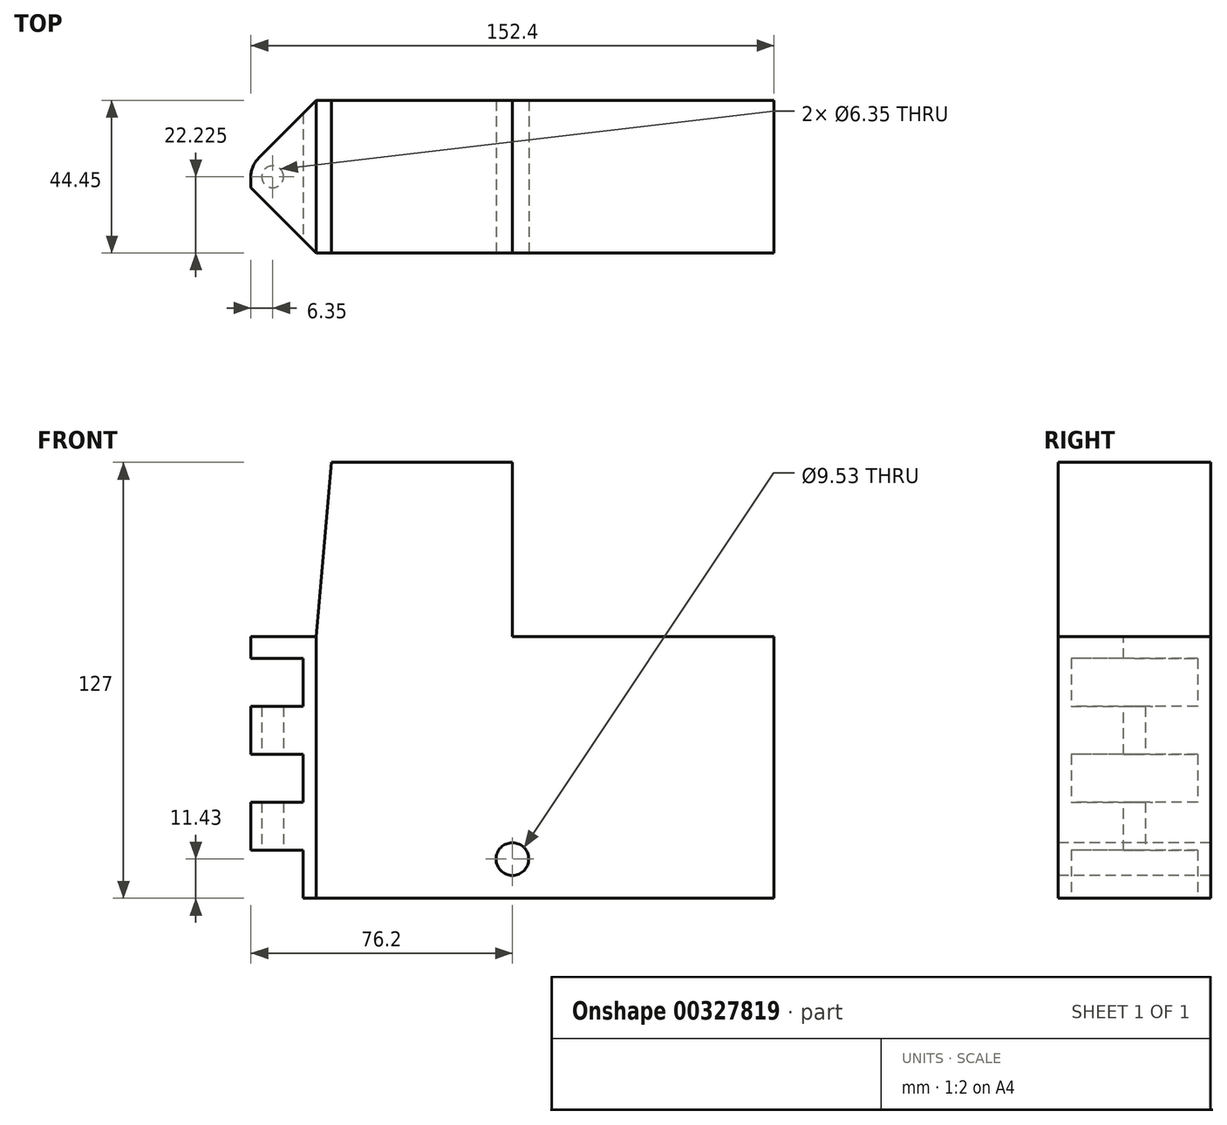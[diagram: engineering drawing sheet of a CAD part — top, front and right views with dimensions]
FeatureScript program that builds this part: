
annotation { "Feature Type Name" : "Feature", "Feature Type Description" : "" }
export const myFeature = defineFeature(function(context is Context, id is Id, definition is map)
    precondition{}
    {
        {
            var Q0;
            Q0=qCreatedBy(makeId("Front.planeOp"),FACE);
            var sketch = newSketch(context, id + "F0", { "sketchPlane" : qUnion([Q0])});
            skLineSegment(sketch, "E0.bottom", {"start": v(0, 0) * mm, "end": v(152.4, 0) * mm});
            skLineSegment(sketch, "E0.top", {"start": v(0, 76.2) * mm, "end": v(152.4, 76.2) * mm});
            skLineSegment(sketch, "E0.left", {"start": v(0, 0) * mm, "end": v(0, 76.2) * mm});
            skLineSegment(sketch, "E0.right", {"start": v(152.4, 0) * mm, "end": v(152.4, 76.2) * mm});
            skSolve(sketch);
        }
        {
            var Q0;
            Q0 = qSketchRegion(id + "F0", true);
            extrude(context, id + "F1", {"entities" : qUnion([Q0]), "depth" : 44.45 * mm});
        }
        {
            var Q0;
            Q0=makeQuery(id+"F1.opExtrude","CAP_FACE",FACE,{"disambiguationData":[OSD([sQuery(id+"F0.wireOp",EDGE,"E0.bottom"),sQuery(id+"F0.wireOp",EDGE,"E0.top"),sQuery(id+"F0.wireOp",EDGE,"E0.left"),sQuery(id+"F0.wireOp",EDGE,"E0.right")])],"isStart":false});
            var sketch = newSketch(context, id + "F2", { "sketchPlane" : qUnion([Q0])});
            skLineSegment(sketch, "E1.0", {"start": v(0, 0) * mm, "end": v(0, 76.2) * mm, "construction": true});
            skLineSegment(sketch, "E2.bottom", {"start": v(0, 0) * mm, "end": v(15.24, 0) * mm});
            skLineSegment(sketch, "E2.top", {"start": v(0, 13.97) * mm, "end": v(15.24, 13.97) * mm});
            skLineSegment(sketch, "E2.left", {"start": v(0, 0) * mm, "end": v(0, 13.97) * mm});
            skLineSegment(sketch, "E2.right", {"start": v(15.24, 0) * mm, "end": v(15.24, 13.97) * mm});
            skLineSegment(sketch, "E3.bottom", {"start": v(0, 27.94) * mm, "end": v(15.24, 27.94) * mm});
            skLineSegment(sketch, "E3.top", {"start": v(0, 41.91) * mm, "end": v(15.24, 41.91) * mm});
            skLineSegment(sketch, "E3.left", {"start": v(0, 27.94) * mm, "end": v(0, 41.91) * mm});
            skLineSegment(sketch, "E3.right", {"start": v(15.24, 27.94) * mm, "end": v(15.24, 41.91) * mm});
            skLineSegment(sketch, "E4.bottom", {"start": v(0, 55.88) * mm, "end": v(15.24, 55.88) * mm});
            skLineSegment(sketch, "E4.top", {"start": v(0, 69.85) * mm, "end": v(15.24, 69.85) * mm});
            skLineSegment(sketch, "E4.left", {"start": v(0, 55.88) * mm, "end": v(0, 69.85) * mm});
            skLineSegment(sketch, "E4.right", {"start": v(15.24, 55.88) * mm, "end": v(15.24, 69.85) * mm});
            skSolve(sketch);
        }
        {
            var Q0;
            Q0 = qSketchRegion(id + "F2", true);
            extrude(context, id + "F3", {"entities" : qUnion([Q0]), "operationType" : NewBodyOperationType.REMOVE, "endBound" : BoundingType.THROUGH_ALL, "oppositeDirection" : true, "depth" : 25.4 * mm});
        }
        {
            var Q0;
            Q0=makeQuery(id+"F1.opExtrude","SWEPT_FACE",FACE,{"disambiguationData":[OSD([sQuery(id+"F0.wireOp",EDGE,"E0.bottom")])]});
            var sketch = newSketch(context, id + "F4", { "sketchPlane" : qUnion([Q0])});
            skCircle(sketch, "E5", {"center": v(6.35, 22.23) * mm, "radius": 3.18 * mm});
            skSolve(sketch);
        }
        {
            var Q0;
            Q0 = qSketchRegion(id + "F4", true);
            extrude(context, id + "F5", {"entities" : qUnion([Q0]), "operationType" : NewBodyOperationType.REMOVE, "oppositeDirection" : true, "depth" : 69.85 * mm});
        }
        {
            var Q0;
            {var subQ0=sQuery(id+"F0.wireOp",EDGE,"E0.left");var subQ1=sQuery(id+"F0.wireOp",EDGE,"E0.top");Q0=makeQuery(id+"F3.boolean.opBoolean","SPLIT",EDGE,{"disambiguationData":[TD([makeQuery(id+"F1.opExtrude","SWEPT_FACE",FACE,{"disambiguationData":[OSD([subQ1])]})])],"derivedFrom":makeQuery(id+"F1.opExtrude","CAP_EDGE",EDGE,{"disambiguationData":[OSD([subQ0])],"isStart":false})});}
            var Q1;
            {var subQ0=sQuery(id+"F0.wireOp",EDGE,"E0.left");Q1=makeQuery(id+"F3.boolean.opBoolean","SPLIT",EDGE,{"disambiguationData":[TD([makeQuery(id+"F3.opExtrude","SWEPT_FACE",FACE,{"disambiguationData":[OSD([sQuery(id+"F2.wireOp",EDGE,"E3.top")])]})])],"derivedFrom":makeQuery(id+"F1.opExtrude","CAP_EDGE",EDGE,{"disambiguationData":[OSD([subQ0])],"isStart":false})});}
            var Q2;
            {var subQ0=sQuery(id+"F0.wireOp",EDGE,"E0.left");Q2=makeQuery(id+"F3.boolean.opBoolean","SPLIT",EDGE,{"disambiguationData":[TD([makeQuery(id+"F3.opExtrude","SWEPT_FACE",FACE,{"disambiguationData":[OSD([sQuery(id+"F2.wireOp",EDGE,"E2.top")])]})])],"derivedFrom":makeQuery(id+"F1.opExtrude","CAP_EDGE",EDGE,{"disambiguationData":[OSD([subQ0])],"isStart":false})});}
            var Q3;
            {var subQ0=sQuery(id+"F0.wireOp",EDGE,"E0.left");Q3=makeQuery(id+"F3.boolean.opBoolean","SPLIT",EDGE,{"disambiguationData":[TD([makeQuery(id+"F3.opExtrude","SWEPT_FACE",FACE,{"disambiguationData":[OSD([sQuery(id+"F2.wireOp",EDGE,"E2.top")])]})])],"derivedFrom":makeQuery(id+"F1.opExtrude","CAP_EDGE",EDGE,{"disambiguationData":[OSD([subQ0])],"isStart":true})});}
            var Q4;
            {var subQ0=sQuery(id+"F0.wireOp",EDGE,"E0.left");Q4=makeQuery(id+"F3.boolean.opBoolean","SPLIT",EDGE,{"disambiguationData":[TD([makeQuery(id+"F3.opExtrude","SWEPT_FACE",FACE,{"disambiguationData":[OSD([sQuery(id+"F2.wireOp",EDGE,"E3.top")])]})])],"derivedFrom":makeQuery(id+"F1.opExtrude","CAP_EDGE",EDGE,{"disambiguationData":[OSD([subQ0])],"isStart":true})});}
            var Q5;
            {var subQ0=sQuery(id+"F0.wireOp",EDGE,"E0.left");var subQ1=sQuery(id+"F0.wireOp",EDGE,"E0.top");Q5=makeQuery(id+"F3.boolean.opBoolean","SPLIT",EDGE,{"disambiguationData":[TD([makeQuery(id+"F1.opExtrude","SWEPT_FACE",FACE,{"disambiguationData":[OSD([subQ1])]})])],"derivedFrom":makeQuery(id+"F1.opExtrude","CAP_EDGE",EDGE,{"disambiguationData":[OSD([subQ0])],"isStart":true})});}
            chamfer(context, id + "F6", {"entities" : qUnion([Q0, Q1, Q2, Q3, Q4, Q5]), "width" : 19.05 * mm, "tangentPropagation" : true});
        }
        {
            var Q0;
            Q0=makeQuery(id+"F1.opExtrude","CAP_FACE",FACE,{"disambiguationData":[OSD([sQuery(id+"F0.wireOp",EDGE,"E0.bottom"),sQuery(id+"F0.wireOp",EDGE,"E0.top"),sQuery(id+"F0.wireOp",EDGE,"E0.left"),sQuery(id+"F0.wireOp",EDGE,"E0.right")])],"isStart":false});
            var sketch = newSketch(context, id + "F7", { "sketchPlane" : qUnion([Q0])});
            skCircle(sketch, "E6", {"center": v(76.2, 11.43) * mm, "radius": 4.76 * mm});
            skSolve(sketch);
        }
        {
            var Q0;
            Q0 = qSketchRegion(id + "F7", true);
            extrude(context, id + "F8", {"entities" : qUnion([Q0]), "operationType" : NewBodyOperationType.REMOVE, "endBound" : BoundingType.THROUGH_ALL, "oppositeDirection" : true, "depth" : 25.4 * mm});
        }
        {
            var Q0;
            Q0=makeQuery(id+"F1.opExtrude","CAP_FACE",FACE,{"disambiguationData":[OSD([sQuery(id+"F0.wireOp",EDGE,"E0.bottom"),sQuery(id+"F0.wireOp",EDGE,"E0.top"),sQuery(id+"F0.wireOp",EDGE,"E0.left"),sQuery(id+"F0.wireOp",EDGE,"E0.right")])],"isStart":false});
            var sketch = newSketch(context, id + "F9", { "sketchPlane" : qUnion([Q0])});
            skLineSegment(sketch, "E7.0", {"start": v(19.05, 76.2) * mm, "end": v(76.2, 76.2) * mm});
            skLineSegment(sketch, "E8", {"start": v(19.05, 76.2) * mm, "end": v(23.5, 127) * mm});
            skLineSegment(sketch, "E9", {"start": v(23.5, 127) * mm, "end": v(76.2, 127) * mm});
            skLineSegment(sketch, "E10", {"start": v(76.2, 127) * mm, "end": v(76.2, 76.2) * mm});
            skPoint(sketch, "E11.orphan", {"position": v(152.4, 76.2) * mm});
            skSolve(sketch);
        }
        {
            var Q0;
            Q0 = qSketchRegion(id + "F9", true);
            extrude(context, id + "F10", {"entities" : qUnion([Q0]), "operationType" : NewBodyOperationType.ADD, "oppositeDirection" : true, "depth" : 44.45 * mm});
        }
        {
            var Q0;
            {var subQ1=sQuery(id+"F0.wireOp",EDGE,"E0.left");var subQ2=sQuery(id+"F0.wireOp",EDGE,"E0.top");var subQ5=makeQuery(id+"F1.opExtrude","SWEPT_FACE",FACE,{"disambiguationData":[OSD([subQ1])]});Q0=makeQuery(id+"F6.opChamfer","BLEND_EDGE",EDGE,{"blendedFrom":[makeQuery(id+"F3.boolean.opBoolean","SPLIT",EDGE,{"disambiguationData":[TD([makeQuery(id+"F3.opExtrude","SWEPT_FACE",FACE,{"disambiguationData":[OSD([sQuery(id+"F2.wireOp",EDGE,"E2.top")])]})])],"derivedFrom":makeQuery(id+"F1.opExtrude","CAP_EDGE",EDGE,{"disambiguationData":[OSD([subQ1])],"isStart":true})}),makeQuery(id+"F3.boolean.opBoolean","SPLIT",FACE,{"disambiguationData":[TD([makeQuery(id+"F1.opExtrude","SWEPT_FACE",FACE,{"disambiguationData":[OSD([subQ2])]})])],"derivedFrom":subQ5})],"blendedInto":[makeQuery(id+"F3.boolean.opBoolean","SPLIT",FACE,{"disambiguationData":[TD([makeQuery(id+"F1.opExtrude","SWEPT_FACE",FACE,{"disambiguationData":[OSD([subQ2])]})])],"derivedFrom":subQ5})]});}
            var Q1;
            {var subQ1=sQuery(id+"F0.wireOp",EDGE,"E0.left");var subQ2=sQuery(id+"F0.wireOp",EDGE,"E0.top");var subQ5=makeQuery(id+"F1.opExtrude","SWEPT_FACE",FACE,{"disambiguationData":[OSD([subQ2])]});var subQ7=makeQuery(id+"F1.opExtrude","SWEPT_FACE",FACE,{"disambiguationData":[OSD([subQ1])]});Q1=makeQuery(id+"F6.opChamfer","BLEND_EDGE",EDGE,{"blendedFrom":[makeQuery(id+"F3.boolean.opBoolean","SPLIT",EDGE,{"disambiguationData":[TD([subQ5])],"derivedFrom":makeQuery(id+"F1.opExtrude","CAP_EDGE",EDGE,{"disambiguationData":[OSD([subQ1])],"isStart":false})}),makeQuery(id+"F3.boolean.opBoolean","SPLIT",FACE,{"disambiguationData":[TD([subQ5])],"derivedFrom":subQ7})],"blendedInto":[makeQuery(id+"F3.boolean.opBoolean","SPLIT",FACE,{"disambiguationData":[TD([subQ5])],"derivedFrom":subQ7})]});}
            var Q2;
            {var subQ1=sQuery(id+"F0.wireOp",EDGE,"E0.left");var subQ2=sQuery(id+"F0.wireOp",EDGE,"E0.top");var subQ5=makeQuery(id+"F1.opExtrude","SWEPT_FACE",FACE,{"disambiguationData":[OSD([subQ1])]});Q2=makeQuery(id+"F6.opChamfer","BLEND_EDGE",EDGE,{"blendedFrom":[makeQuery(id+"F3.boolean.opBoolean","SPLIT",EDGE,{"disambiguationData":[TD([makeQuery(id+"F1.opExtrude","SWEPT_FACE",FACE,{"disambiguationData":[OSD([subQ2])]})])],"derivedFrom":makeQuery(id+"F1.opExtrude","CAP_EDGE",EDGE,{"disambiguationData":[OSD([subQ1])],"isStart":false})}),makeQuery(id+"F3.boolean.opBoolean","SPLIT",FACE,{"disambiguationData":[TD([makeQuery(id+"F3.opExtrude","SWEPT_FACE",FACE,{"disambiguationData":[OSD([sQuery(id+"F2.wireOp",EDGE,"E3.top")])]})])],"derivedFrom":subQ5})],"blendedInto":[makeQuery(id+"F3.boolean.opBoolean","SPLIT",FACE,{"disambiguationData":[TD([makeQuery(id+"F3.opExtrude","SWEPT_FACE",FACE,{"disambiguationData":[OSD([sQuery(id+"F2.wireOp",EDGE,"E3.top")])]})])],"derivedFrom":subQ5})]});}
            var Q3;
            {var subQ1=sQuery(id+"F0.wireOp",EDGE,"E0.left");var subQ5=makeQuery(id+"F1.opExtrude","SWEPT_FACE",FACE,{"disambiguationData":[OSD([subQ1])]});Q3=makeQuery(id+"F6.opChamfer","BLEND_EDGE",EDGE,{"blendedFrom":[makeQuery(id+"F3.boolean.opBoolean","SPLIT",EDGE,{"disambiguationData":[TD([makeQuery(id+"F3.opExtrude","SWEPT_FACE",FACE,{"disambiguationData":[OSD([sQuery(id+"F2.wireOp",EDGE,"E2.top")])]})])],"derivedFrom":makeQuery(id+"F1.opExtrude","CAP_EDGE",EDGE,{"disambiguationData":[OSD([subQ1])],"isStart":true})}),makeQuery(id+"F3.boolean.opBoolean","SPLIT",FACE,{"disambiguationData":[TD([makeQuery(id+"F3.opExtrude","SWEPT_FACE",FACE,{"disambiguationData":[OSD([sQuery(id+"F2.wireOp",EDGE,"E3.top")])]})])],"derivedFrom":subQ5})],"blendedInto":[makeQuery(id+"F3.boolean.opBoolean","SPLIT",FACE,{"disambiguationData":[TD([makeQuery(id+"F3.opExtrude","SWEPT_FACE",FACE,{"disambiguationData":[OSD([sQuery(id+"F2.wireOp",EDGE,"E3.top")])]})])],"derivedFrom":subQ5})]});}
            var Q4;
            {var subQ1=sQuery(id+"F0.wireOp",EDGE,"E0.left");var subQ5=makeQuery(id+"F3.opExtrude","SWEPT_FACE",FACE,{"disambiguationData":[OSD([sQuery(id+"F2.wireOp",EDGE,"E2.top")])]});var subQ7=makeQuery(id+"F1.opExtrude","SWEPT_FACE",FACE,{"disambiguationData":[OSD([subQ1])]});Q4=makeQuery(id+"F6.opChamfer","BLEND_EDGE",EDGE,{"blendedFrom":[makeQuery(id+"F3.boolean.opBoolean","SPLIT",EDGE,{"disambiguationData":[TD([subQ5])],"derivedFrom":makeQuery(id+"F1.opExtrude","CAP_EDGE",EDGE,{"disambiguationData":[OSD([subQ1])],"isStart":true})}),makeQuery(id+"F3.boolean.opBoolean","SPLIT",FACE,{"disambiguationData":[TD([subQ5])],"derivedFrom":subQ7})],"blendedInto":[makeQuery(id+"F3.boolean.opBoolean","SPLIT",FACE,{"disambiguationData":[TD([subQ5])],"derivedFrom":subQ7})]});}
            var Q5;
            {var subQ1=sQuery(id+"F0.wireOp",EDGE,"E0.left");var subQ2=sQuery(id+"F0.wireOp",EDGE,"E0.top");var subQ5=makeQuery(id+"F1.opExtrude","SWEPT_FACE",FACE,{"disambiguationData":[OSD([subQ1])]});Q5=makeQuery(id+"F6.opChamfer","BLEND_EDGE",EDGE,{"blendedFrom":[makeQuery(id+"F3.boolean.opBoolean","SPLIT",EDGE,{"disambiguationData":[TD([makeQuery(id+"F1.opExtrude","SWEPT_FACE",FACE,{"disambiguationData":[OSD([subQ2])]})])],"derivedFrom":makeQuery(id+"F1.opExtrude","CAP_EDGE",EDGE,{"disambiguationData":[OSD([subQ1])],"isStart":false})}),makeQuery(id+"F3.boolean.opBoolean","SPLIT",FACE,{"disambiguationData":[TD([makeQuery(id+"F3.opExtrude","SWEPT_FACE",FACE,{"disambiguationData":[OSD([sQuery(id+"F2.wireOp",EDGE,"E2.top")])]})])],"derivedFrom":subQ5})],"blendedInto":[makeQuery(id+"F3.boolean.opBoolean","SPLIT",FACE,{"disambiguationData":[TD([makeQuery(id+"F3.opExtrude","SWEPT_FACE",FACE,{"disambiguationData":[OSD([sQuery(id+"F2.wireOp",EDGE,"E2.top")])]})])],"derivedFrom":subQ5})]});}
            fillet(context, id + "F11", {"entities" : qUnion([Q0, Q1, Q2, Q3, Q4, Q5]), "radius" : 7.62 * mm, "tangentPropagation" : true, "allowEdgeOverflow" : false});
        }
    });
